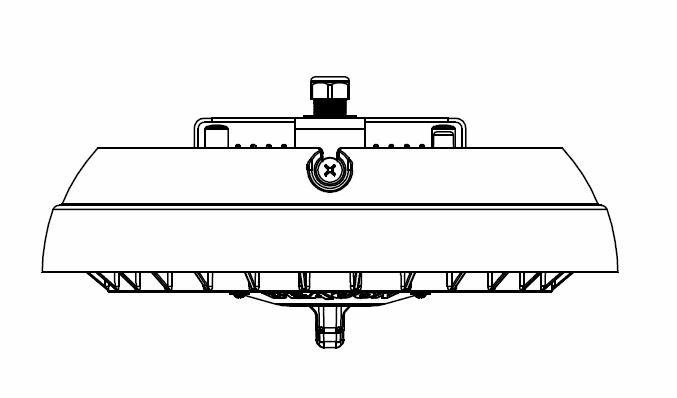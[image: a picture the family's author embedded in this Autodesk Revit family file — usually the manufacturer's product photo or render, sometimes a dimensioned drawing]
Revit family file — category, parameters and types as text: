
# Revit family: ORB
name_source: partatom
category: Lighting Fixtures
revit_build: Autodesk Revit Architecture 2012 (Build: 20110309_2315(x64)
units: mm (PartAtom-declared; Revit-internal decimal feet)

## types (1)
- ORB
    Apparent Load = 0 VA
    Color Filter = 16777215
    Default Elevation = 48 "
    Description = Orbeon is a commercial grade LED parking garage and canopy downlight which utilizes high powered LEDs, precise efficient optical control, and features
application versatility through integrated intelligent control options.
    Dimming Lamp Color Temperature Shift = <None>
    Emit Shape Visible in Rendering = No
    Emit from Circle Diameter = 24 "
    Lamp = LED Lamp
    Light Bulb Material = Hubbell - Glass
    Manufacturer = Beacon Lighting
    Manufacturer Fax = 941-751-5535
    Model = Orbeon
    Nominal Watts = 0 W
    Photometric Web File = generic
    Tilt Angle = -90.00°
    URL = http://www.beaconproducts.com
    Voltage = 120 - 277V
    Wattage Comments = 60W, 18 Nichia 2198 Lamps

## geometry (parser evidence)
native form markers: Blend x8, Sweep x5
no freeform markers — native parametric forms only
